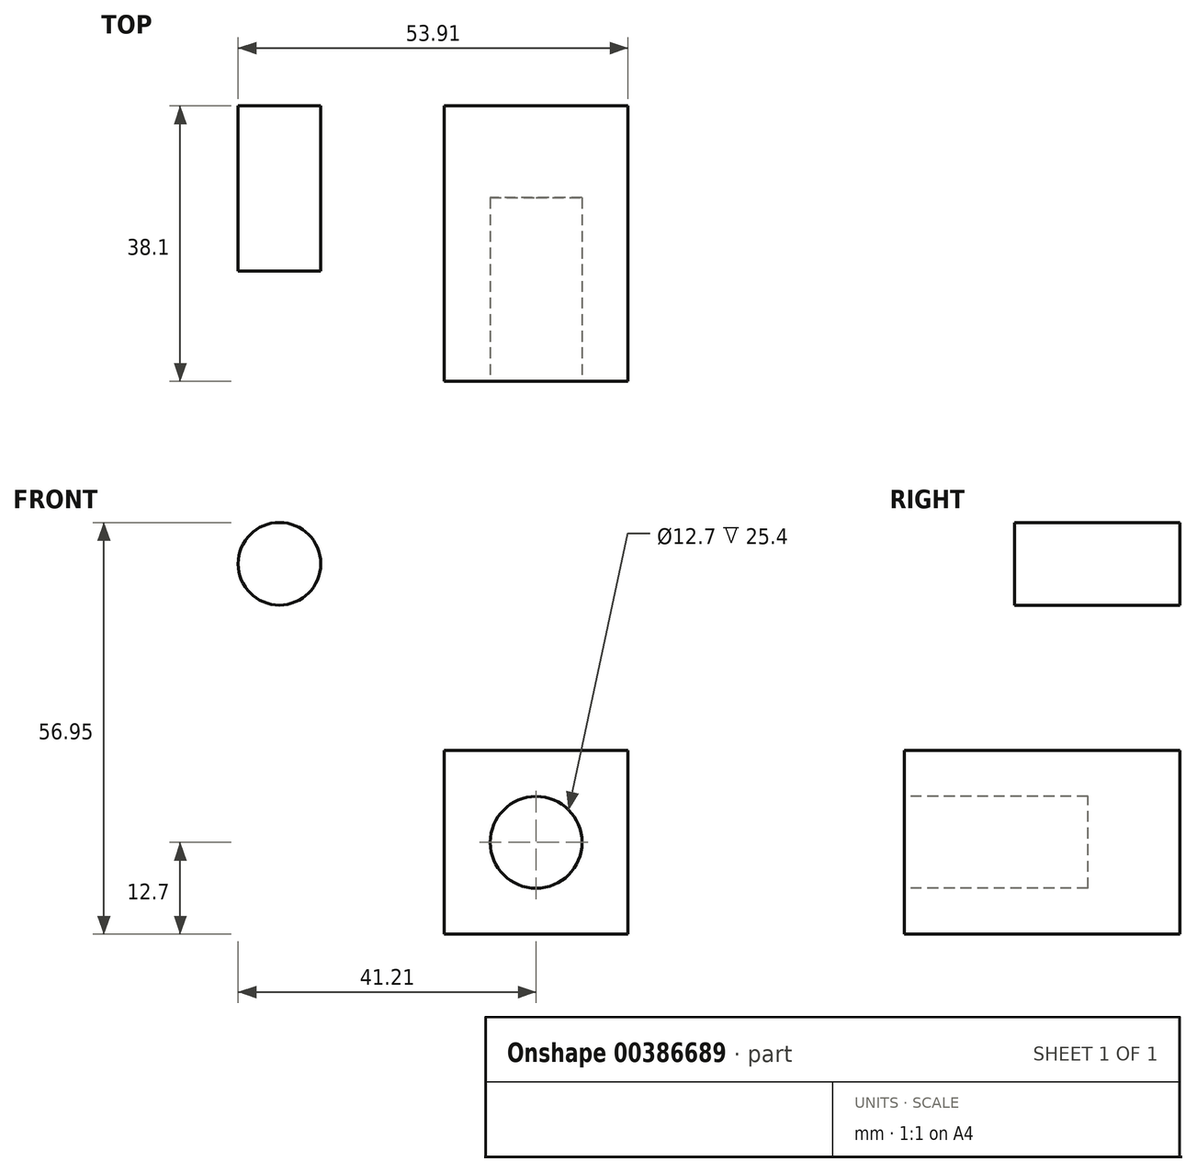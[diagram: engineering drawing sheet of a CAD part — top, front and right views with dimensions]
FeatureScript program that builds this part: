
annotation { "Feature Type Name" : "Feature", "Feature Type Description" : "" }
export const myFeature = defineFeature(function(context is Context, id is Id, definition is map)
    precondition{}
    {
        {
            var Q0;
            Q0=qCreatedBy(makeId("Front.planeOp"),FACE);
            var sketch = newSketch(context, id + "F0", { "sketchPlane" : qUnion([Q0])});
            skLineSegment(sketch, "E0.bottom", {"start": v(12.7, -12.7) * mm, "end": v(-12.7, -12.7) * mm});
            skLineSegment(sketch, "E0.top", {"start": v(12.7, 12.7) * mm, "end": v(-12.7, 12.7) * mm});
            skLineSegment(sketch, "E0.left", {"start": v(12.7, -12.7) * mm, "end": v(12.7, 12.7) * mm});
            skLineSegment(sketch, "E0.right", {"start": v(-12.7, -12.7) * mm, "end": v(-12.7, 12.7) * mm});
            skPoint(sketch, "E0.middle", {"position": v(0, 0) * mm});
            skSolve(sketch);
        }
        {
            var Q0;
            Q0=makeQuery(id+"F0.imprint","IMPRINT",FACE,{"disambiguationData":[TD([[makeQuery(id+"F0.imprint","IMPRINT",EDGE,{"derivedFrom":sQuery(id+"F0.wireOp",EDGE,"E0.bottom")}),-1.0]])]});
            extrude(context, id + "F1", {"entities" : qUnion([Q0]), "depth" : 38.1 * mm});
        }
        {
            var Q0;
            Q0=makeQuery(id+"F1.opExtrude","CAP_FACE",FACE,{"disambiguationData":[OSD([sQuery(id+"F0.wireOp",EDGE,"E0.bottom"),sQuery(id+"F0.wireOp",EDGE,"E0.top"),sQuery(id+"F0.wireOp",EDGE,"E0.left"),sQuery(id+"F0.wireOp",EDGE,"E0.right")])],"isStart":false});
            var sketch = newSketch(context, id + "F2", { "sketchPlane" : qUnion([Q0])});
            skCircle(sketch, "E1", {"center": v(0, 0) * mm, "radius": 6.35 * mm});
            skSolve(sketch);
        }
        {
            var Q0;
            Q0=makeQuery(id+"F2.imprint","IMPRINT",FACE,{"disambiguationData":[TD([[makeQuery(id+"F2.imprint","IMPRINT",EDGE,{"derivedFrom":sQuery(id+"F2.wireOp",EDGE,"E1")}),1.0]])]});
            extrude(context, id + "F3", {"entities" : qUnion([Q0]), "operationType" : NewBodyOperationType.REMOVE, "oppositeDirection" : true, "depth" : 25.4 * mm});
        }
        {
            var Q0;
            Q0=qCreatedBy(makeId("Front.planeOp"),FACE);
            var sketch = newSketch(context, id + "F4", { "sketchPlane" : qUnion([Q0])});
            skCircle(sketch, "E2", {"center": v(-35.5, 38.53) * mm, "radius": 5.72 * mm});
            skSolve(sketch);
        }
        {
            var Q0;
            Q0=makeQuery(id+"F4.imprint","IMPRINT",FACE,{"disambiguationData":[TD([[makeQuery(id+"F4.imprint","IMPRINT",EDGE,{"derivedFrom":sQuery(id+"F4.wireOp",EDGE,"E2")}),1.0]])]});
            extrude(context, id + "F5", {"entities" : qUnion([Q0]), "depth" : 22.86 * mm});
        }
    });
